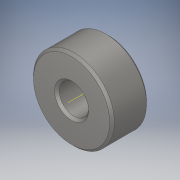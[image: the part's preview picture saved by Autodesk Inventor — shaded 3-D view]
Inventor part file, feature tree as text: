
AUTODESK INVENTOR PART (.ipt)
format: ipt  version: 2019.4 (Build 234330000, 330)  size: 120,832 bytes
history: native  units: in
note: dims shown in document units (in); Inventor stores cm internally (conversion verified against a paired STEP export)
features: plane x2, extrude x1, chamfer x1, sketch x1
ambient origin geometry x8: Origin, YZ Plane, XZ Plane, XY Plane, X Axis, Y Axis, Z Axis, Center Point
bodies: Solid1 (feature_tree)
feature tree (5):
  extrude  "Extrusion1"  Depth=0.125in TaperAngle=45.0deg
  chamfer  "Chamfer1"  Distance=0.25in
  plane  "Work Plane1"
  plane  "Work Plane2"
  sketch  "Sketch1"  dims[d2=0.3125in d3=0.0in d4=0.02in d5=0.125in d6=45.0deg d7=0.25in d8=0.6875in]
